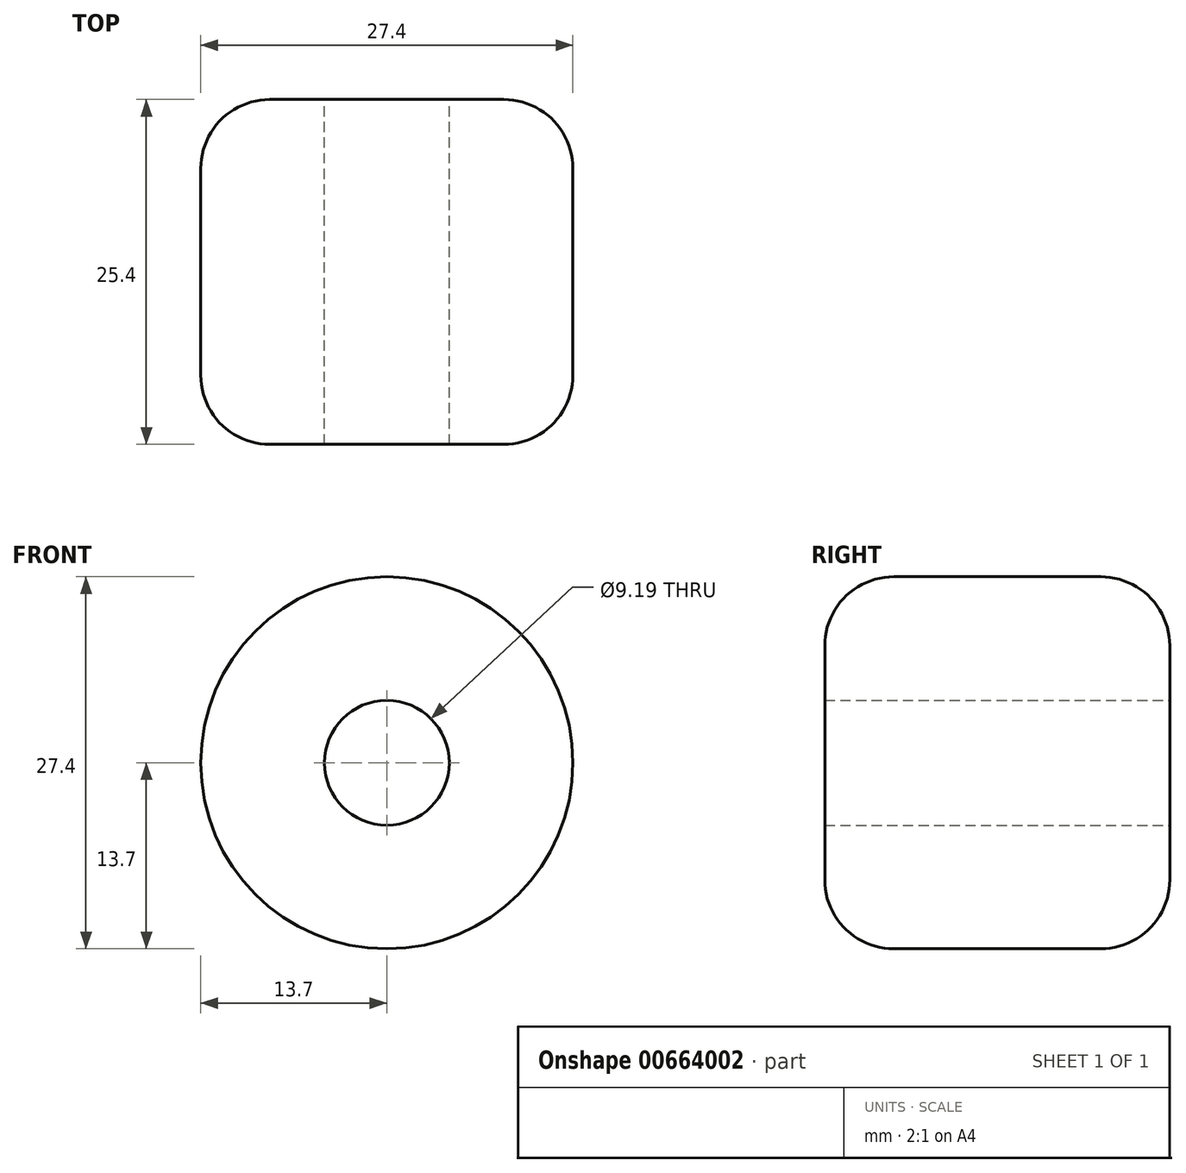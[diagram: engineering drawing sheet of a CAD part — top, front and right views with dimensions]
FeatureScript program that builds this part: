
annotation { "Feature Type Name" : "Feature", "Feature Type Description" : "" }
export const myFeature = defineFeature(function(context is Context, id is Id, definition is map)
    precondition{}
    {
        {
            var Q0;
            Q0=qCreatedBy(makeId("Front.planeOp"),FACE);
            var sketch = newSketch(context, id + "F0", { "sketchPlane" : qUnion([Q0])});
            skCircle(sketch, "E0", {"center": v(0, 0) * mm, "radius": 13.7 * mm});
            skCircle(sketch, "E1", {"center": v(0, 0) * mm, "radius": 4.6 * mm});
            skLineSegment(sketch, "E2", {"start": v(0, 13.7) * mm, "end": v(0, 4.6) * mm});
            skLineSegment(sketch, "E3", {"start": v(13.7, 0) * mm, "end": v(4.6, 0) * mm});
            skLineSegment(sketch, "E4", {"start": v(-13.7, 0) * mm, "end": v(-4.6, 0) * mm});
            skLineSegment(sketch, "E5", {"start": v(0, -4.6) * mm, "end": v(0, -13.7) * mm});
            skLineSegment(sketch, "E6", {"start": v(0, -13.7) * mm, "end": v(0, -13.7) * mm});
            skSolve(sketch);
        }
        {
            var Q0;
            {var subQ0=sQuery(id+"F0.wireOp",EDGE,"E2");Q0=makeQuery(id+"F0.imprint","IMPRINT",FACE,{"disambiguationData":[TD([[makeQuery(id+"F0.imprint","IMPRINT",EDGE,{"derivedFrom":subQ0}),1.0]])]});}
            var Q1;
            {var subQ0=sQuery(id+"F0.wireOp",EDGE,"E2");Q1=makeQuery(id+"F0.imprint","IMPRINT",FACE,{"disambiguationData":[TD([[makeQuery(id+"F0.imprint","IMPRINT",EDGE,{"derivedFrom":subQ0}),-1.0]])]});}
            var Q2;
            {var subQ0=sQuery(id+"F0.wireOp",EDGE,"E3");Q2=makeQuery(id+"F0.imprint","IMPRINT",FACE,{"disambiguationData":[TD([[makeQuery(id+"F0.imprint","IMPRINT",EDGE,{"derivedFrom":subQ0}),1.0]])]});}
            var Q3;
            {var subQ0=sQuery(id+"F0.wireOp",EDGE,"E4");Q3=makeQuery(id+"F0.imprint","IMPRINT",FACE,{"disambiguationData":[TD([[makeQuery(id+"F0.imprint","IMPRINT",EDGE,{"derivedFrom":subQ0}),-1.0]])]});}
            extrude(context, id + "F1", {"entities" : qUnion([Q0, Q1, Q2, Q3]), "endBound" : BoundingType.SYMMETRIC, "depth" : 25.4 * mm, "offsetDistance" : 25.4 * mm});
        }
        {
            var Q0;
            Q0=makeQuery(id+"F1.opExtrude","CAP_EDGE",EDGE,{"disambiguationData":[OSD([sQuery(id+"F0.wireOp",EDGE,"E0")])],"isStart":false});
            var Q1;
            Q1=makeQuery(id+"F1.opExtrude","CAP_EDGE",EDGE,{"disambiguationData":[OSD([sQuery(id+"F0.wireOp",EDGE,"E0")])],"isStart":true});
            fillet(context, id + "F2", {"entities" : qUnion([Q0, Q1]), "radius" : 5.08 * mm, "tangentPropagation" : true, "allowEdgeOverflow" : false});
        }
    });
